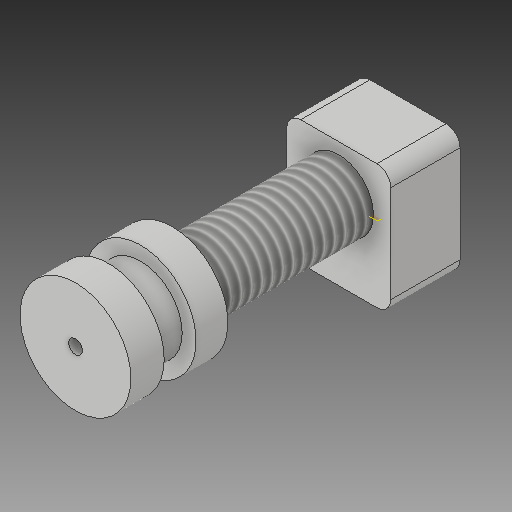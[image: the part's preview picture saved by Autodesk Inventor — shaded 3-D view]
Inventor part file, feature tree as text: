
AUTODESK INVENTOR PART (.ipt)
format: ipt  version: 2017 (Build 210142000, 142)  size: 185,344 bytes
history: native  units: mm
features: sketch x10, other x3, plane x1
ambient origin geometry x8: Origin, YZ Plane, XZ Plane, XY Plane, X Axis, Y Axis, Z Axis, Center Point
bodies: Solid1 (feature_tree)
feature tree (14):
  other  "Hotend Mock Up_MIR.ipt"
  other  "Solid1::Hotend Mock Up_MIR.ipt"
  other  "TaggingFeature1"
  sketch  "Sketch1"  dims[d0=10.0mm]
  sketch  "Sketch2"
  sketch  "Sketch3"
  sketch  "Sketch4"
  sketch  "Sketch5"
  sketch  "Sketch6"
  sketch  "Sketch7"
  sketch  "Sketch8"
  sketch  "Sketch9"
  sketch  "Sketch10"
  plane  "Work Plane1"
